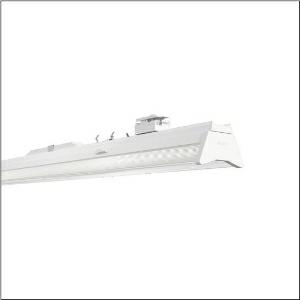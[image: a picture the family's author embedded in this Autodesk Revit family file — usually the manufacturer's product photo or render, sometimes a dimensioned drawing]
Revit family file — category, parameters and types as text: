
# Revit family: licross_r__11_performance_ho_51tm16mn4gxm_a288
name_source: partatom
category: Lighting Fixtures
units: mm (PartAtom-declared; Revit-internal decimal feet)

## family parameters
Cut with Voids When Loaded = No
Host = Face
Light Source = No
Part Type = Normal
Room Calculation Point = No
Round Connector Dimension = Use Diameter
Shared = No

## types (1)
- --- (1 x LED, 16020 lm, 87.4 W, 4000K)
    Apparent Load = 87 VA
    CIE Flux Codes = 63 87 95 78 100
    Color Rendering = 80
    Color Temperature = 4000K
    Default Elevation = 1800 mm
    Description = Licross® 11 Performance HO, luminaire insert, of sheet steel, galvanised, coil coated, white, length: 1.500mm, width: 120mm, height: 123mm, LED rated luminous flux: 16.020lm, light colour: 840, control gear: ON/OFF Multilumen, with plug, 3-pole, with phase selection, mains connection: 220..240V, AC, 50/60Hz, rated input power: 87W, internal wiring halogen-free, primary light control with lens, of plastic, primary optical cover: cover, of PMMA, light emission: direct/indirect distribution, primary light characteristic: symmetric, protection rating (complete): IP40, insulation class (complete): insulation class I (protective earthing), certification: CE, ENEC, VDE, UKCA, protection symbol: D if used in an environment without relevant dust loads with corresponding accessories, impact resistance: IK06, permissible ambient temperature for indoor applications: -35..+35°C, corresponds to IFS (International Featured Standards) requirements for safety and quality in the food industry, reducing of maximum allowable ambient temperature of 5°C with ceiling mounting, LABS conformity tested according to VDMA 24364:2018-05, packaging unit: 1 piece
    Height = 114 mm
    Lamp = 1 x LED
    Lamp Light Flux = 16020 lm
    Lamp Power = 87.4 W
    Lamp count = 1
    Length = 1500 mm
    Luminous efficacy = 183 lm/W
    Manufacturer = Siteco
    ModVariant = No
    Model = 51TM16MN4GXM
    Mounting Place = Ceiling
    Mounting Type = Pendant
    Number of Poles = 1
    OnlyDefault = Yes
    Power Factor = 1
    Product Name = Licross® 11 Performance HO
    Product group = luminaire insert | ceiling pendant
    ProductGroupID = 902
    Protection Class = Protection class I
    Protection Degree = IP 40
    RLX_Detail_Level = 1
    RLX_Emergency_Light_Flux = 0 lm
    RLX_Emergency_Type = 0
    RLX_Emergency_Type_DB = No
    RlxData = <blob elided: 31801 chars, md5=755c38c4>
    Socket = socket
    Standby Power = 0 W
    System Light Flux = 16020 lm
    System Power = 87 W
    Type Comments = factory setting: luminous flux: 100 % | (A | C | E) | 203 mA
    Type Image = l_1256138.jpg
    URL = http://relux.com
    VarID = @adj_107745
    Voltage = 0 V
    Weight = 0.00 kg
    Width = 120 mm

## geometry (parser evidence)
native form markers: Blend x4, Sweep x13
no freeform markers — native parametric forms only
